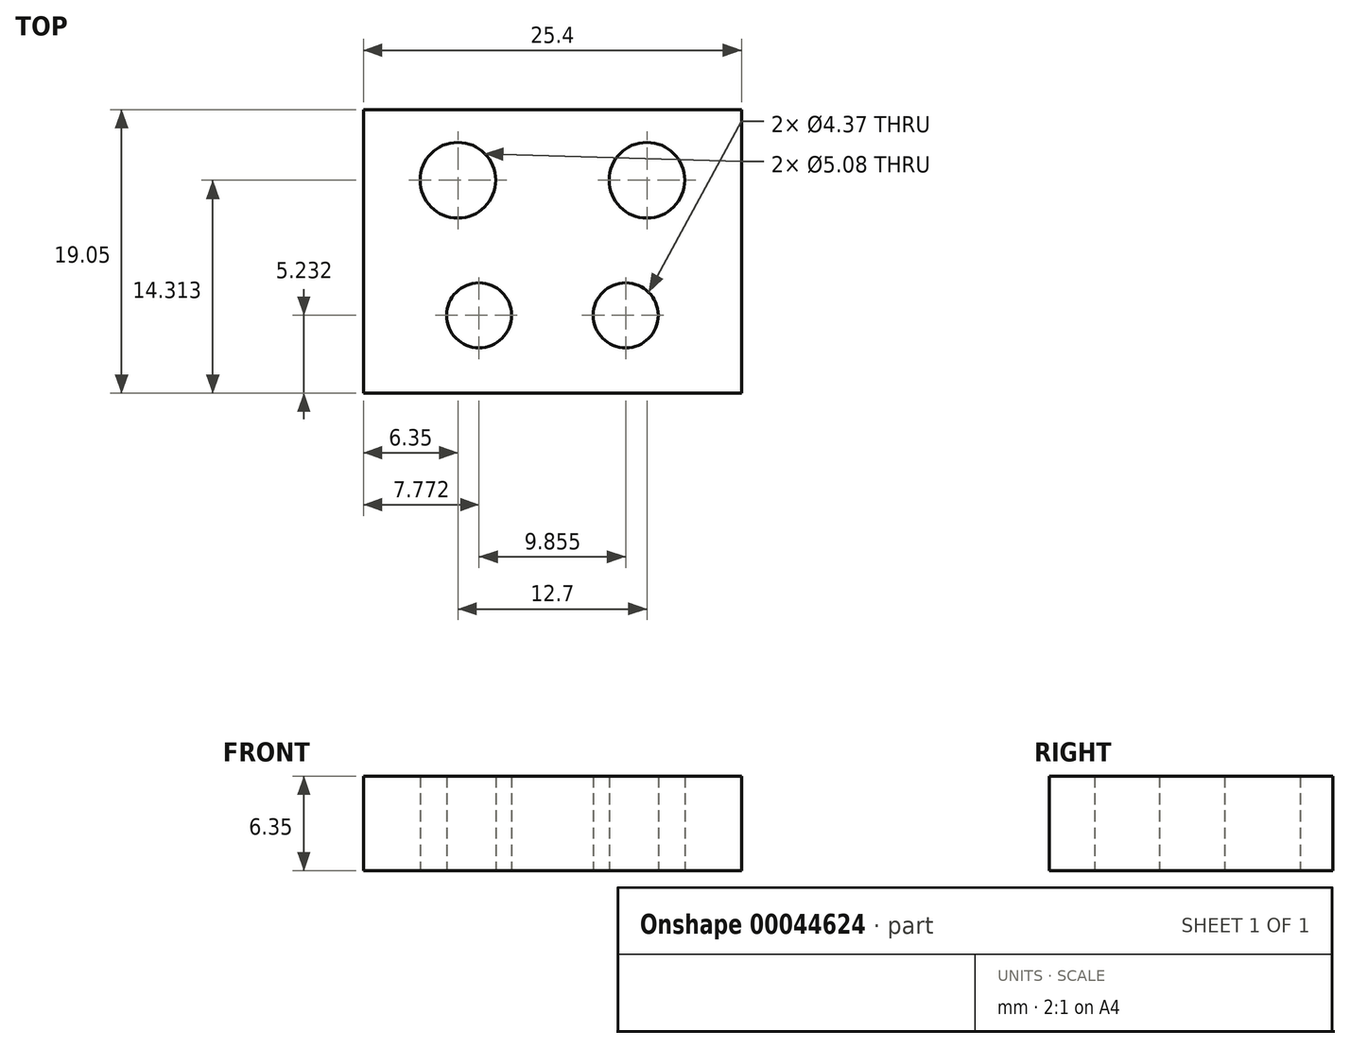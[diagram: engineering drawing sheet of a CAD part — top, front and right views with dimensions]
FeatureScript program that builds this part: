
annotation { "Feature Type Name" : "Feature", "Feature Type Description" : "" }
export const myFeature = defineFeature(function(context is Context, id is Id, definition is map)
    precondition{}
    {
        {
            var Q0;
            Q0=qCreatedBy(makeId("Top.planeOp"),FACE);
            var sketch = newSketch(context, id + "F0", { "sketchPlane" : qUnion([Q0])});
            skLineSegment(sketch, "E0.bottom", {"start": v(-12.7, 19.05) * mm, "end": v(12.7, 19.05) * mm});
            skLineSegment(sketch, "E0.top", {"start": v(-12.7, 0) * mm, "end": v(12.7, 0) * mm});
            skLineSegment(sketch, "E0.left", {"start": v(-12.7, 19.05) * mm, "end": v(-12.7, 0) * mm});
            skLineSegment(sketch, "E0.right", {"start": v(12.7, 19.05) * mm, "end": v(12.7, 0) * mm});
            skLineSegment(sketch, "E1", {"start": v(-12.7, 5.23) * mm, "end": v(12.7, 5.23) * mm});
            skCircle(sketch, "E2", {"center": v(-4.93, 5.23) * mm, "radius": 2.18 * mm});
            skCircle(sketch, "E3", {"center": v(4.93, 5.23) * mm, "radius": 2.18 * mm});
            skLineSegment(sketch, "E4", {"start": v(-12.7, 9.52) * mm, "end": v(12.7, 9.52) * mm});
            skLineSegment(sketch, "E5", {"start": v(-12.7, 14.31) * mm, "end": v(12.7, 14.31) * mm});
            skCircle(sketch, "E6", {"center": v(-6.35, 14.31) * mm, "radius": 2.54 * mm});
            skCircle(sketch, "E7", {"center": v(6.35, 14.31) * mm, "radius": 2.54 * mm});
            skSolve(sketch);
        }
        {
            var Q0;
            {var subQ8=sQuery(id+"F0.wireOp",EDGE,"E0.bottom");Q0=makeQuery(id+"F0.imprint","IMPRINT",FACE,{"disambiguationData":[TD([[makeQuery(id+"F0.imprint","IMPRINT",EDGE,{"derivedFrom":subQ8}),-1.0]])]});}
            var Q1;
            {var subQ11=sQuery(id+"F0.wireOp",EDGE,"E4");Q1=makeQuery(id+"F0.imprint","IMPRINT",FACE,{"disambiguationData":[TD([[makeQuery(id+"F0.imprint","IMPRINT",EDGE,{"derivedFrom":subQ11}),1.0]])]});}
            var Q2;
            {var subQ0=sQuery(id+"F0.wireOp",EDGE,"E4");Q2=makeQuery(id+"F0.imprint","IMPRINT",FACE,{"disambiguationData":[TD([[makeQuery(id+"F0.imprint","IMPRINT",EDGE,{"derivedFrom":subQ0}),-1.0]])]});}
            var Q3;
            {var subQ6=sQuery(id+"F0.wireOp",EDGE,"E0.top");Q3=makeQuery(id+"F0.imprint","IMPRINT",FACE,{"disambiguationData":[TD([[makeQuery(id+"F0.imprint","IMPRINT",EDGE,{"derivedFrom":subQ6}),1.0]])]});}
            extrude(context, id + "F1", {"entities" : qUnion([Q0, Q1, Q2, Q3]), "depth" : 6.35 * mm});
        }
    });
